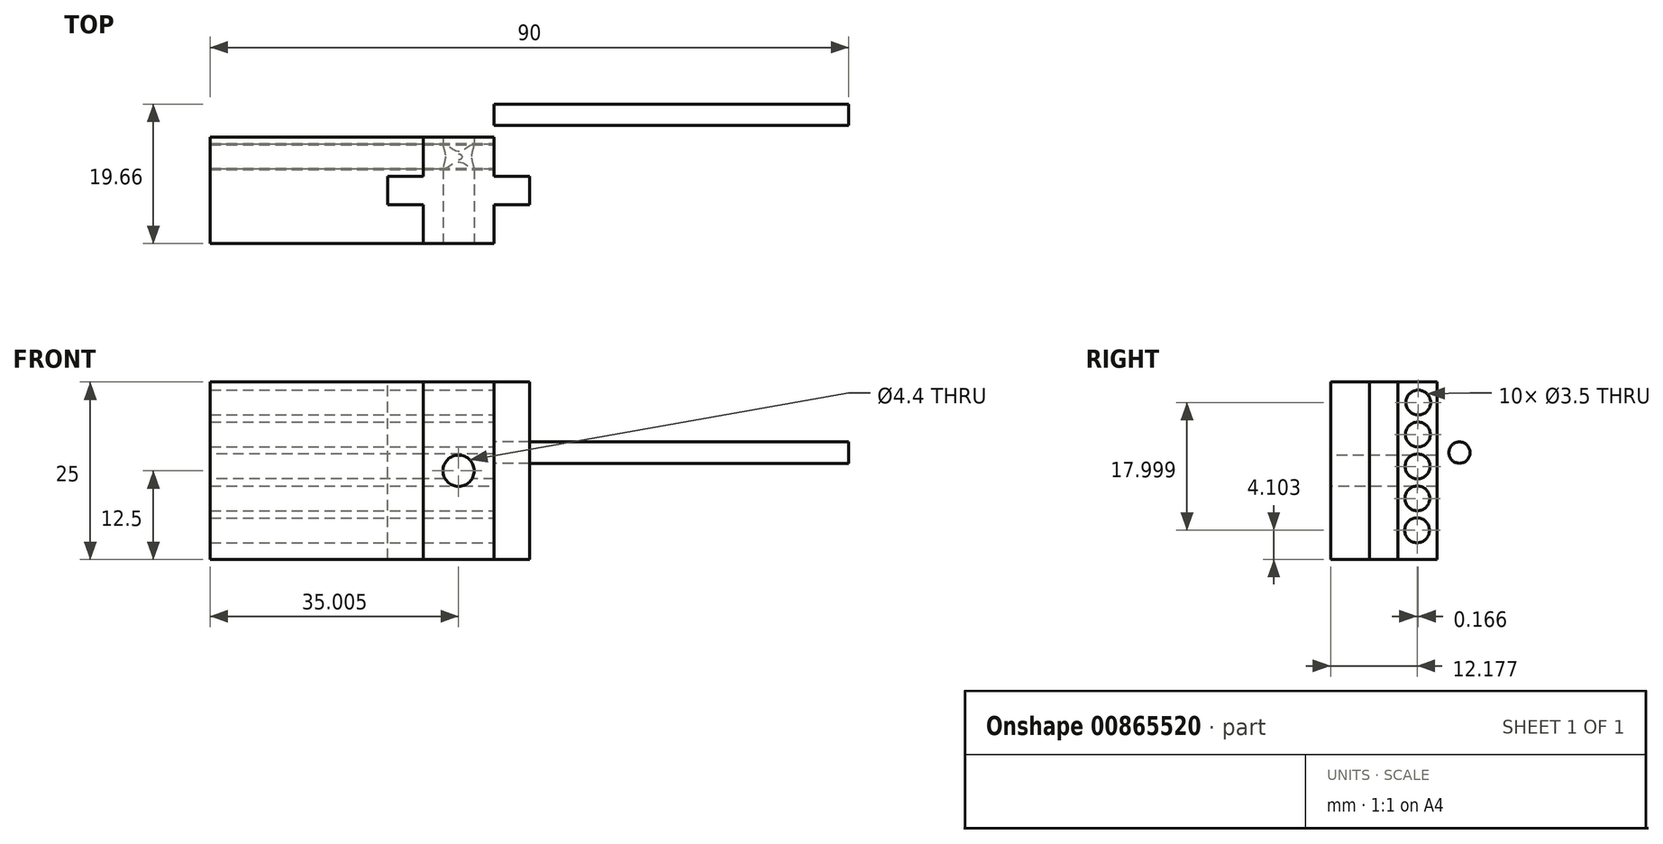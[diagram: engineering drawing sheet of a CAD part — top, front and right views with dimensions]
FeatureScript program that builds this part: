
annotation { "Feature Type Name" : "Feature", "Feature Type Description" : "" }
export const myFeature = defineFeature(function(context is Context, id is Id, definition is map)
    precondition{}
    {
        {
            var Q0;
            Q0=qCreatedBy(makeId("Top.planeOp"),FACE);
            var sketch = newSketch(context, id + "F0", { "sketchPlane" : qUnion([Q0])});
            skLineSegment(sketch, "E0", {"start": v(-51.5, -16.6) * mm, "end": v(-51.5, -31.6) * mm});
            skLineSegment(sketch, "E1", {"start": v(-51.5, -31.6) * mm, "end": v(-21.5, -31.6) * mm});
            skLineSegment(sketch, "E2", {"start": v(-21.5, -31.6) * mm, "end": v(-21.5, -16.6) * mm});
            skLineSegment(sketch, "E3", {"start": v(-21.5, -16.6) * mm, "end": v(-51.5, -16.6) * mm});
            skSolve(sketch);
        }
        {
            var Q0;
            Q0=makeQuery(id+"F0.imprint","IMPRINT",FACE,{"disambiguationData":[TD([[makeQuery(id+"F0.imprint","IMPRINT",EDGE,{"derivedFrom":sQuery(id+"F0.wireOp",EDGE,"E0")}),1.0]])]});
            extrude(context, id + "F1", {"entities" : qUnion([Q0]), "depth" : 25 * mm, "offsetDistance" : 25 * mm});
        }
        {
            var Q0;
            Q0=makeQuery(id+"F1.opExtrude","CAP_FACE",FACE,{"disambiguationData":[OSD([sQuery(id+"F0.wireOp",EDGE,"E0"),sQuery(id+"F0.wireOp",EDGE,"E1"),sQuery(id+"F0.wireOp",EDGE,"E2"),sQuery(id+"F0.wireOp",EDGE,"E3")])],"isStart":false});
            var sketch = newSketch(context, id + "F2", { "sketchPlane" : qUnion([Q0])});
            skPoint(sketch, "E4", {"position": v(-36.5, -24.1) * mm});
            skPoint(sketch, "E4.positionSnap0", {"position": v(-36.5, -16.6) * mm});
            skPoint(sketch, "E4.positionSnap1", {"position": v(-51.5, -24.1) * mm});
            skLineSegment(sketch, "E5", {"start": v(-51.5, -24.1) * mm, "end": v(-21.5, -24.1) * mm, "construction": true});
            skLineSegment(sketch, "E6", {"start": v(-36.5, -16.6) * mm, "end": v(-36.5, -31.6) * mm, "construction": true});
            skLineSegment(sketch, "E7", {"start": v(-21.5, -22.1) * mm, "end": v(-26.5, -22.1) * mm});
            skLineSegment(sketch, "E8", {"start": v(-26.5, -22.1) * mm, "end": v(-26.5, -26.1) * mm});
            skLineSegment(sketch, "E9", {"start": v(-26.5, -26.1) * mm, "end": v(-21.5, -26.1) * mm});
            skSolve(sketch);
        }
        {
            var Q0;
            {var subQ0=sQuery(id+"F2.wireOp",EDGE,"E7");Q0=makeQuery(id+"F2.imprint","IMPRINT",FACE,{"disambiguationData":[TD([[makeQuery(id+"F2.imprint","IMPRINT",EDGE,{"derivedFrom":subQ0}),1.0]])]});}
            extrude(context, id + "F3", {"entities" : qUnion([Q0]), "operationType" : NewBodyOperationType.REMOVE, "endBound" : BoundingType.THROUGH_ALL, "oppositeDirection" : true, "depth" : 25 * mm, "offsetDistance" : 25 * mm});
        }
        {
            var Q0;
            Q0=makeQuery(id+"F1.opExtrude","CAP_FACE",FACE,{"disambiguationData":[OSD([sQuery(id+"F0.wireOp",EDGE,"E0"),sQuery(id+"F0.wireOp",EDGE,"E1"),sQuery(id+"F0.wireOp",EDGE,"E2"),sQuery(id+"F0.wireOp",EDGE,"E3")])],"isStart":false});
            var sketch = newSketch(context, id + "F4", { "sketchPlane" : qUnion([Q0])});
            skLineSegment(sketch, "E10", {"start": v(-21.5, -16.6) * mm, "end": v(-21.5, -22.1) * mm});
            skLineSegment(sketch, "E11", {"start": v(-21.5, -22.1) * mm, "end": v(-26.5, -22.1) * mm});
            skLineSegment(sketch, "E12", {"start": v(-26.5, -22.1) * mm, "end": v(-26.5, -26.1) * mm});
            skLineSegment(sketch, "E13", {"start": v(-26.5, -26.1) * mm, "end": v(-21.5, -26.1) * mm});
            skLineSegment(sketch, "E14", {"start": v(-21.5, -26.1) * mm, "end": v(-21.5, -31.6) * mm});
            skLineSegment(sketch, "E15", {"start": v(-21.5, -31.6) * mm, "end": v(-11.5, -31.6) * mm});
            skLineSegment(sketch, "E16", {"start": v(-11.5, -31.6) * mm, "end": v(-11.5, -26.1) * mm});
            skLineSegment(sketch, "E17", {"start": v(-11.5, -26.1) * mm, "end": v(-6.5, -26.1) * mm});
            skLineSegment(sketch, "E18", {"start": v(-6.5, -26.1) * mm, "end": v(-6.5, -22.1) * mm});
            skLineSegment(sketch, "E19", {"start": v(-6.5, -22.1) * mm, "end": v(-11.5, -22.1) * mm});
            skLineSegment(sketch, "E20", {"start": v(-11.5, -22.1) * mm, "end": v(-11.5, -16.6) * mm});
            skLineSegment(sketch, "E21", {"start": v(-11.5, -16.6) * mm, "end": v(-21.5, -16.6) * mm});
            skSolve(sketch);
        }
        {
            var Q0;
            Q0=makeQuery(id+"F4.imprint","IMPRINT",FACE,{"disambiguationData":[TD([[makeQuery(id+"F4.imprint","IMPRINT",EDGE,{"derivedFrom":sQuery(id+"F4.wireOp",EDGE,"KjGPcjqK-ecES-xzwH-dhJD-s5jw8TqLaLf2")}),1.0]])]});
            var Q1;
            Q1=makeQuery(id+"F4.imprint","IMPRINT",FACE,{"disambiguationData":[TD([[makeQuery(id+"F4.imprint","IMPRINT",EDGE,{"derivedFrom":sQuery(id+"F4.wireOp",EDGE,"E10")}),-1.0]])]});
            extrude(context, id + "F5", {"entities" : qUnion([Q0, Q1]), "oppositeDirection" : true, "depth" : 25 * mm, "offsetDistance" : 25 * mm});
        }
        {
            var Q0;
            Q0=makeQuery(id+"F1.opExtrude","SWEPT_FACE",FACE,{"disambiguationData":[OSD([sQuery(id+"F0.wireOp",EDGE,"E0")])]});
            var sketch = newSketch(context, id + "F6", { "sketchPlane" : qUnion([Q0])});
            skLineSegment(sketch, "E22", {"start": v(22.09, 25) * mm, "end": v(22.09, 0) * mm, "construction": true});
            skLineSegment(sketch, "E23", {"start": v(22.09, 0) * mm, "end": v(16.6, 0) * mm, "construction": true});
            skCircle(sketch, "E24", {"center": v(19.34, 13.1) * mm, "radius": 1.75 * mm});
            skPoint(sketch, "E24.centerSnap0", {"position": v(19.34, 0) * mm});
            skSolve(sketch);
        }
        {
            var Q0;
            Q0=makeQuery(id+"F6.imprint","IMPRINT",FACE,{"disambiguationData":[TD([[makeQuery(id+"F6.imprint","IMPRINT",EDGE,{"derivedFrom":sQuery(id+"F6.wireOp",EDGE,"E24")}),1.0]])]});
            extrude(context, id + "F7", {"entities" : qUnion([Q0]), "operationType" : NewBodyOperationType.REMOVE, "endBound" : BoundingType.THROUGH_ALL, "oppositeDirection" : true, "depth" : 43 * mm, "offsetDistance" : 25 * mm});
        }
        {
            var Q0;
            Q0=makeQuery(id+"F5.opExtrude","SWEPT_FACE",FACE,{"disambiguationData":[OSD([sQuery(id+"F4.wireOp",EDGE,"E20")])]});
            var sketch = newSketch(context, id + "F8", { "sketchPlane" : qUnion([Q0])});
            skCircle(sketch, "E25", {"center": v(-19.34, 13.1) * mm, "radius": 1.75 * mm});
            skCircle(sketch, "E26.1.0.0", {"center": v(-19.3, 17.6) * mm, "radius": 1.75 * mm});
            skCircle(sketch, "E26.2.0.0", {"center": v(-19.26, 22.1) * mm, "radius": 1.75 * mm});
            skLineSegment(sketch, "E26.direction1", {"start": v(-19.34, 13.1) * mm, "end": v(-19.3, 17.6) * mm, "construction": true});
            skCircle(sketch, "E27.1.0.0", {"center": v(-19.38, 8.6) * mm, "radius": 1.75 * mm});
            skLineSegment(sketch, "E27.1.0.1", {"start": v(-19.38, 8.6) * mm, "end": v(-19.34, 13.1) * mm, "construction": true});
            skCircle(sketch, "E27.2.0.0", {"center": v(-19.42, 4.1) * mm, "radius": 1.75 * mm});
            skLineSegment(sketch, "E27.2.0.1", {"start": v(-19.42, 4.1) * mm, "end": v(-19.38, 8.6) * mm, "construction": true});
            skLineSegment(sketch, "E27.direction1", {"start": v(-19.34, 13.1) * mm, "end": v(-19.38, 8.6) * mm, "construction": true});
            skSolve(sketch);
        }
        {
            var Q0;
            Q0=makeQuery(id+"F8.imprint","IMPRINT",FACE,{"disambiguationData":[TD([[makeQuery(id+"F8.imprint","IMPRINT",EDGE,{"derivedFrom":sQuery(id+"F8.wireOp",EDGE,"E26.2.0.0")}),1.0]])]});
            var Q1;
            Q1=makeQuery(id+"F8.imprint","IMPRINT",FACE,{"disambiguationData":[TD([[makeQuery(id+"F8.imprint","IMPRINT",EDGE,{"derivedFrom":sQuery(id+"F8.wireOp",EDGE,"E26.1.0.0")}),1.0]])]});
            var Q2;
            Q2=makeQuery(id+"F8.imprint","IMPRINT",FACE,{"disambiguationData":[TD([[makeQuery(id+"F8.imprint","IMPRINT",EDGE,{"derivedFrom":sQuery(id+"F8.wireOp",EDGE,"E27.1.0.0")}),1.0]])]});
            var Q3;
            Q3=makeQuery(id+"F8.imprint","IMPRINT",FACE,{"disambiguationData":[TD([[makeQuery(id+"F8.imprint","IMPRINT",EDGE,{"derivedFrom":sQuery(id+"F8.wireOp",EDGE,"E27.2.0.0")}),1.0]])]});
            var Q4;
            Q4=sQuery(id+"F8.wireOp",EDGE,"E26.2.0.0");
            extrude(context, id + "F9", {"entities" : qUnion([Q0, Q1, Q2, Q3]), "operationType" : NewBodyOperationType.REMOVE, "surfaceEntities" : qUnion([Q4]), "endBound" : BoundingType.THROUGH_ALL, "oppositeDirection" : true, "depth" : 25 * mm, "offsetDistance" : 25 * mm});
        }
        {
            var Q0;
            Q0=makeQuery(id+"F5.opExtrude","SWEPT_FACE",FACE,{"disambiguationData":[OSD([sQuery(id+"F4.wireOp",EDGE,"E20")])]});
            var sketch = newSketch(context, id + "F10", { "sketchPlane" : qUnion([Q0])});
            skCircle(sketch, "E28", {"center": v(-13.44, 15.05) * mm, "radius": 1.5 * mm});
            skSolve(sketch);
        }
        {
            var Q0;
            Q0=makeQuery(id+"F10.imprint","IMPRINT",FACE,{"disambiguationData":[TD([[makeQuery(id+"F10.imprint","IMPRINT",EDGE,{"derivedFrom":sQuery(id+"F10.wireOp",EDGE,"E28")}),1.0]])]});
            extrude(context, id + "F11", {"entities" : qUnion([Q0]), "depth" : 50 * mm, "offsetDistance" : 25 * mm});
        }
        {
            var Q0;
            Q0=makeQuery(id+"F5.opExtrude","SWEPT_FACE",FACE,{"disambiguationData":[OSD([sQuery(id+"F4.wireOp",EDGE,"E15")])]});
            var sketch = newSketch(context, id + "F12", { "sketchPlane" : qUnion([Q0])});
            skCircle(sketch, "E29", {"center": v(-16.5, 12.5) * mm, "radius": 4 * mm});
            skPoint(sketch, "E29.centerSnap0", {"position": v(-11.5, 12.5) * mm});
            skPoint(sketch, "E29.centerSnap1", {"position": v(-16.5, 25) * mm});
            skSolve(sketch);
        }
        {
            var Q0;
            Q0=sQuery(id+"F12.wireOp",VERTEX,"E29.center");
            var Q1;
            Q1=makeQuery(id+"F5.opExtrude","SWEPT_BODY",BODY,{"disambiguationData":[OSD([sQuery(id+"F4.wireOp",EDGE,"E10"),sQuery(id+"F4.wireOp",EDGE,"E11"),sQuery(id+"F4.wireOp",EDGE,"E12"),sQuery(id+"F4.wireOp",EDGE,"E13"),sQuery(id+"F4.wireOp",EDGE,"E14"),sQuery(id+"F4.wireOp",EDGE,"E15"),sQuery(id+"F4.wireOp",EDGE,"E16"),sQuery(id+"F4.wireOp",EDGE,"E17"),sQuery(id+"F4.wireOp",EDGE,"E18"),sQuery(id+"F4.wireOp",EDGE,"E19"),sQuery(id+"F4.wireOp",EDGE,"E20"),sQuery(id+"F4.wireOp",EDGE,"E21")])]});
            hole(context, id + "F13", {"style" : HoleStyle.SIMPLE, "endStyle" : HoleEndStyle.THROUGH, "standardTappedOrClearance" : lookupTablePath({ "fit" : "Normal", "standard" : "ISO", "size" : "M4", "type" : "Clearance" }), "standardBlindInLast" : lookupTablePath({ "fit" : "Standard", "standard" : "ISO", "size" : "M4", "type" : "Clearance" }), "holeDiameter" : 4.4 * mm, "majorDiameter" : 5 * mm, "isTappedThrough" : true, "tappedDepth" : 12 * mm, "tapClearance" : 3, "locations" : qUnion([Q0]), "scope" : qUnion([Q1])});
        }
    });
